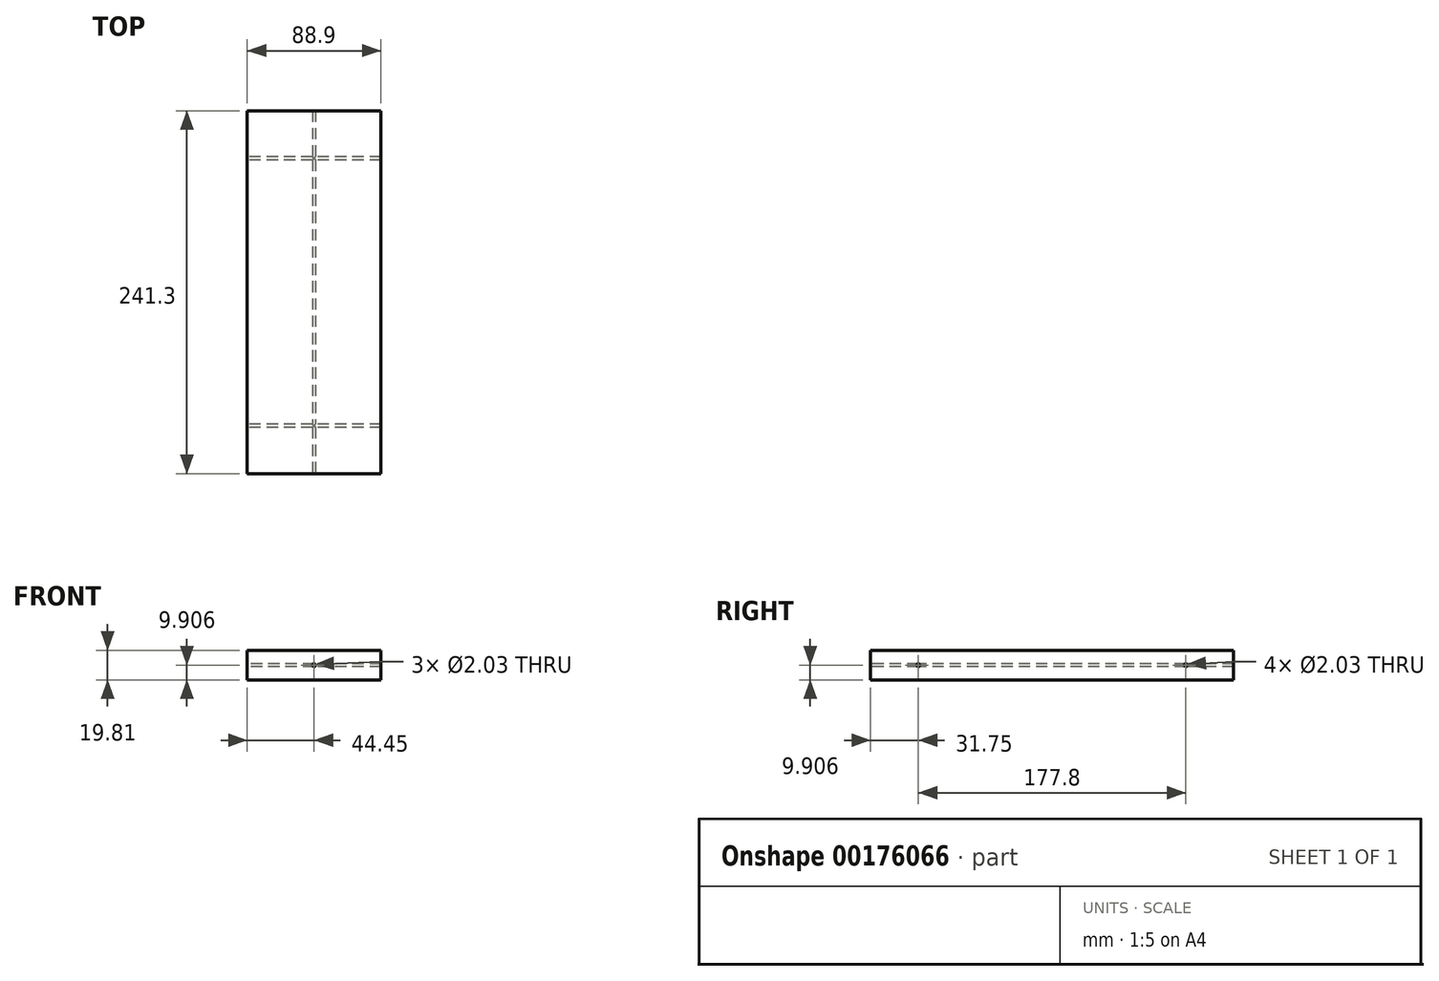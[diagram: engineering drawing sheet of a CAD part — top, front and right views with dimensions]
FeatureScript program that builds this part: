
annotation { "Feature Type Name" : "Feature", "Feature Type Description" : "" }
export const myFeature = defineFeature(function(context is Context, id is Id, definition is map)
    precondition{}
    {
        {
            var Q0;
            Q0=qCreatedBy(makeId("Top.planeOp"),FACE);
            var sketch = newSketch(context, id + "F0", { "sketchPlane" : qUnion([Q0])});
            skLineSegment(sketch, "E0.bottom", {"start": v(0, 0) * mm, "end": v(88.9, 0) * mm});
            skLineSegment(sketch, "E0.top", {"start": v(0, 241.3) * mm, "end": v(88.9, 241.3) * mm});
            skLineSegment(sketch, "E0.left", {"start": v(0, 0) * mm, "end": v(0, 241.3) * mm});
            skLineSegment(sketch, "E0.right", {"start": v(88.9, 0) * mm, "end": v(88.9, 241.3) * mm});
            skSolve(sketch);
        }
        {
            var Q0;
            Q0=makeQuery(id+"F0.imprint","IMPRINT",FACE,{"disambiguationData":[TD([[makeQuery(id+"F0.imprint","IMPRINT",EDGE,{"derivedFrom":sQuery(id+"F0.wireOp",EDGE,"E0.bottom")}),1.0]])]});
            extrude(context, id + "F1", {"entities" : qUnion([Q0]), "depth" : 19.8 * mm});
        }
        {
            var Q0;
            Q0=makeQuery(id+"F1.opExtrude","SWEPT_FACE",FACE,{"disambiguationData":[OSD([sQuery(id+"F0.wireOp",EDGE,"E0.bottom")])]});
            var sketch = newSketch(context, id + "F2", { "sketchPlane" : qUnion([Q0])});
            skCircle(sketch, "E1", {"center": v(44.45, 9.9) * mm, "radius": 1.02 * mm});
            skSolve(sketch);
        }
        {
            var Q0;
            Q0 = qSketchRegion(id + "F2", true);
            extrude(context, id + "F3", {"entities" : qUnion([Q0]), "operationType" : NewBodyOperationType.REMOVE, "endBound" : BoundingType.THROUGH_ALL, "oppositeDirection" : true, "depth" : 25.4 * mm});
        }
        {
            var Q0;
            Q0=makeQuery(id+"F1.opExtrude","SWEPT_FACE",FACE,{"disambiguationData":[OSD([sQuery(id+"F0.wireOp",EDGE,"E0.left")])]});
            var sketch = newSketch(context, id + "F4", { "sketchPlane" : qUnion([Q0])});
            skCircle(sketch, "E2", {"center": v(-209.55, 9.9) * mm, "radius": 1.02 * mm});
            skCircle(sketch, "E3", {"center": v(-31.75, 9.9) * mm, "radius": 1.02 * mm});
            skPoint(sketch, "E4", {"position": v(-120.65, 19.81) * mm});
            skSolve(sketch);
        }
        {
            var Q0;
            Q0 = qSketchRegion(id + "F4", true);
            extrude(context, id + "F5", {"entities" : qUnion([Q0]), "operationType" : NewBodyOperationType.REMOVE, "endBound" : BoundingType.THROUGH_ALL, "oppositeDirection" : true, "depth" : 25.4 * mm});
        }
    });
